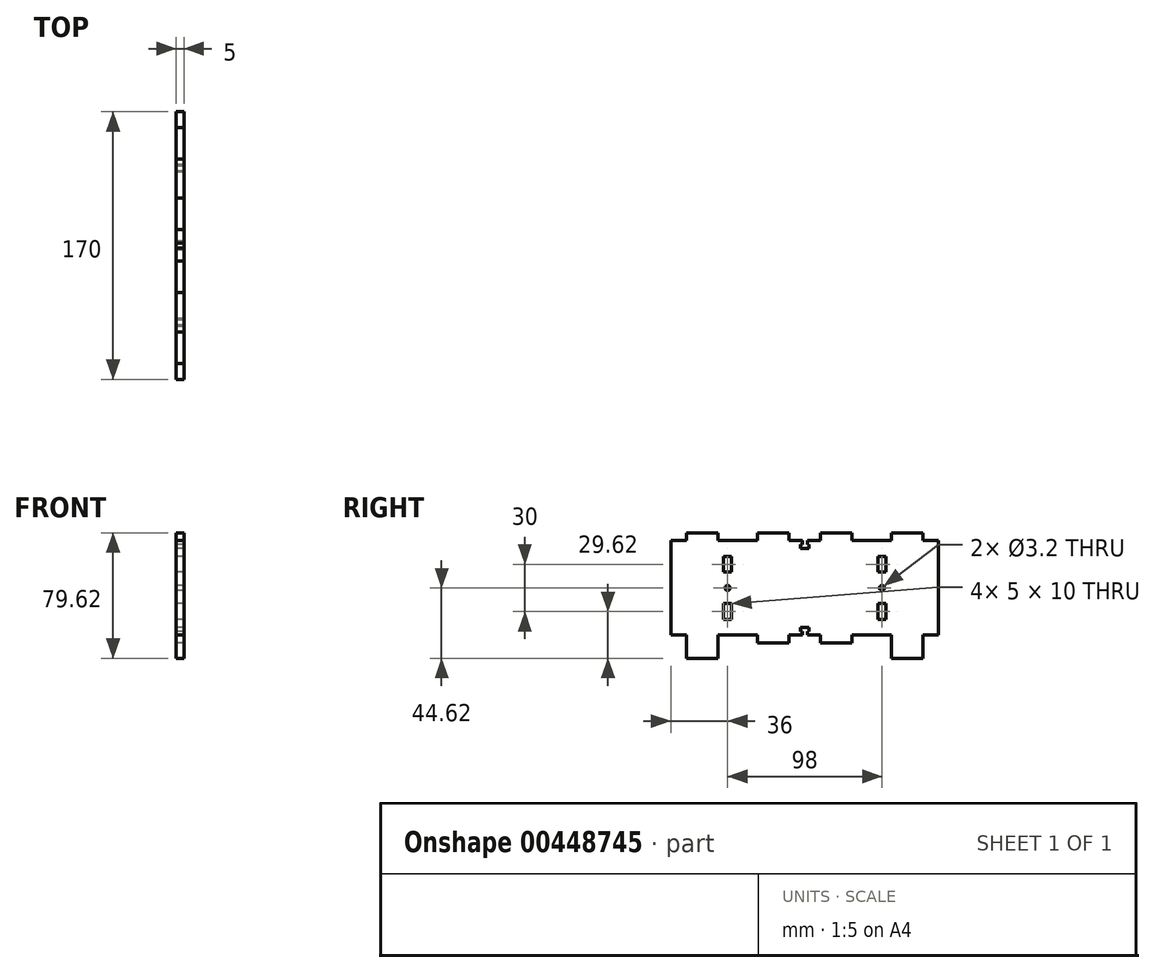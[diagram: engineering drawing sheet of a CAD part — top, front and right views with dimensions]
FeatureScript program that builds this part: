
annotation { "Feature Type Name" : "Feature", "Feature Type Description" : "" }
export const myFeature = defineFeature(function(context is Context, id is Id, definition is map)
    precondition{}
    {
        {
            assignVariable(context, id + "F0", {"name" : "thickness", "anyValue" : 5 * mm});
        }
        {
            var Q0;
            Q0=qCreatedBy(makeId("Right.planeOp"),FACE);
            var sketch = newSketch(context, id + "F1", { "sketchPlane" : qUnion([Q0])});
            skLineSegment(sketch, "E0.bottom", {"start": v(0, 0) * mm, "end": v(83.4, 0) * mm});
            skLineSegment(sketch, "E0.top", {"start": v(0, 60) * mm, "end": v(83.4, 60) * mm});
            skLineSegment(sketch, "E0.left", {"start": v(0, 0) * mm, "end": v(0, 60) * mm});
            skLineSegment(sketch, "E0.right", {"start": v(170, 0) * mm, "end": v(170, 60) * mm});
            skLineSegment(sketch, "E1", {"start": v(10, 0) * mm, "end": v(10, -14.62) * mm});
            skLineSegment(sketch, "E2", {"start": v(10, -14.62) * mm, "end": v(30, -14.62) * mm});
            skLineSegment(sketch, "E3", {"start": v(30, -14.62) * mm, "end": v(30, 0) * mm});
            skLineSegment(sketch, "E4", {"start": v(55, 0) * mm, "end": v(55, -5) * mm});
            skLineSegment(sketch, "E5", {"start": v(55, -5) * mm, "end": v(75, -5) * mm});
            skLineSegment(sketch, "E6", {"start": v(75, -5) * mm, "end": v(75, 0) * mm});
            skLineSegment(sketch, "E7", {"start": v(85, 60) * mm, "end": v(85, 0) * mm, "construction": true});
            skLineSegment(sketch, "E8.MirrorCS", {"start": v(95, -5) * mm, "end": v(95, 0) * mm});
            skLineSegment(sketch, "E9.MirrorCS", {"start": v(115, -5) * mm, "end": v(95, -5) * mm});
            skLineSegment(sketch, "E10.MirrorCS", {"start": v(115, 0) * mm, "end": v(115, -5) * mm});
            skLineSegment(sketch, "E11.MirrorCS", {"start": v(140, -14.62) * mm, "end": v(140, 0) * mm});
            skLineSegment(sketch, "E12.MirrorCS", {"start": v(160, -14.62) * mm, "end": v(140, -14.62) * mm});
            skLineSegment(sketch, "E13.MirrorCS", {"start": v(160, 0) * mm, "end": v(160, -14.62) * mm});
            skLineSegment(sketch, "E14", {"start": v(83.4, 0) * mm, "end": v(83.4, 2.5) * mm});
            skLineSegment(sketch, "E15", {"start": v(83.4, 2.5) * mm, "end": v(82.25, 2.5) * mm});
            skLineSegment(sketch, "E16", {"start": v(82.25, 2.5) * mm, "end": v(82.25, 5) * mm});
            skLineSegment(sketch, "E17", {"start": v(82.25, 5) * mm, "end": v(85, 5) * mm});
            skLineSegment(sketch, "E18.MirrorCS", {"start": v(86.6, 2.5) * mm, "end": v(87.75, 2.5) * mm});
            skLineSegment(sketch, "E19.MirrorCS", {"start": v(87.75, 5) * mm, "end": v(85, 5) * mm});
            skLineSegment(sketch, "E20.MirrorCS", {"start": v(87.75, 2.5) * mm, "end": v(87.75, 5) * mm});
            skLineSegment(sketch, "E21.MirrorCS", {"start": v(86.6, 0) * mm, "end": v(86.6, 2.5) * mm});
            skLineSegment(sketch, "E22", {"start": v(0, 30) * mm, "end": v(170, 30) * mm, "construction": true});
            skLineSegment(sketch, "E23.MirrorCS", {"start": v(83.4, 57.5) * mm, "end": v(82.25, 57.5) * mm});
            skLineSegment(sketch, "E24.MirrorCS", {"start": v(87.75, 57.5) * mm, "end": v(87.75, 55) * mm});
            skLineSegment(sketch, "E25.MirrorCS", {"start": v(86.6, 60) * mm, "end": v(86.6, 57.5) * mm});
            skLineSegment(sketch, "E26.MirrorCS", {"start": v(86.6, 57.5) * mm, "end": v(87.75, 57.5) * mm});
            skLineSegment(sketch, "E27.MirrorCS", {"start": v(82.25, 57.5) * mm, "end": v(82.25, 55) * mm});
            skLineSegment(sketch, "E28.MirrorCS", {"start": v(83.4, 60) * mm, "end": v(83.4, 57.5) * mm});
            skLineSegment(sketch, "E29.MirrorCS", {"start": v(82.25, 55) * mm, "end": v(85, 55) * mm});
            skLineSegment(sketch, "E30.MirrorCS", {"start": v(87.75, 55) * mm, "end": v(85, 55) * mm});
            skLineSegment(sketch, "E31.MirrorCS", {"start": v(95, 65) * mm, "end": v(95, 60) * mm});
            skLineSegment(sketch, "E32.MirrorCS", {"start": v(75, 65) * mm, "end": v(75, 60) * mm});
            skLineSegment(sketch, "E33.MirrorCS", {"start": v(55, 60) * mm, "end": v(55, 65) * mm});
            skLineSegment(sketch, "E34.MirrorCS", {"start": v(115, 60) * mm, "end": v(115, 65) * mm});
            skLineSegment(sketch, "E35.MirrorCS", {"start": v(115, 65) * mm, "end": v(95, 65) * mm});
            skLineSegment(sketch, "E36.MirrorCS", {"start": v(55, 65) * mm, "end": v(75, 65) * mm});
            skLineSegment(sketch, "E37", {"start": v(10, 60) * mm, "end": v(10, 65) * mm});
            skLineSegment(sketch, "E38", {"start": v(10, 65) * mm, "end": v(30, 65) * mm});
            skLineSegment(sketch, "E39", {"start": v(30, 65) * mm, "end": v(30, 60) * mm});
            skLineSegment(sketch, "E40.MirrorCS", {"start": v(140, 65) * mm, "end": v(140, 60) * mm});
            skLineSegment(sketch, "E41.MirrorCS", {"start": v(160, 60) * mm, "end": v(160, 65) * mm});
            skLineSegment(sketch, "E42.MirrorCS", {"start": v(160, 65) * mm, "end": v(140, 65) * mm});
            skLineSegment(sketch, "E43.trimOffspring", {"start": v(86.6, 0) * mm, "end": v(170, 0) * mm});
            skLineSegment(sketch, "E44.trimOffspring", {"start": v(86.6, 60) * mm, "end": v(170, 60) * mm});
            skLineSegment(sketch, "E45.bottom", {"start": v(33.5, 20) * mm, "end": v(38.5, 20) * mm});
            skLineSegment(sketch, "E45.top", {"start": v(33.5, 10) * mm, "end": v(38.5, 10) * mm});
            skLineSegment(sketch, "E45.left", {"start": v(33.5, 20) * mm, "end": v(33.5, 10) * mm});
            skLineSegment(sketch, "E45.right", {"start": v(38.5, 20) * mm, "end": v(38.5, 10) * mm});
            skCircle(sketch, "E46", {"center": v(36, 30) * mm, "radius": 1.6 * mm});
            skPoint(sketch, "E46.centerSnap0", {"position": v(36, 20) * mm});
            skLineSegment(sketch, "E47.MirrorCS", {"start": v(33.5, 40) * mm, "end": v(38.5, 40) * mm});
            skLineSegment(sketch, "E48.MirrorCS", {"start": v(38.5, 40) * mm, "end": v(38.5, 50) * mm});
            skLineSegment(sketch, "E49.MirrorCS", {"start": v(33.5, 50) * mm, "end": v(38.5, 50) * mm});
            skLineSegment(sketch, "E50.MirrorCS", {"start": v(33.5, 40) * mm, "end": v(33.5, 50) * mm});
            skCircle(sketch, "E51.MirrorC", {"center": v(134, 30) * mm, "radius": 1.6 * mm});
            skLineSegment(sketch, "E52.MirrorCS", {"start": v(136.5, 20) * mm, "end": v(131.5, 20) * mm});
            skLineSegment(sketch, "E53.MirrorCS", {"start": v(131.5, 20) * mm, "end": v(131.5, 10) * mm});
            skLineSegment(sketch, "E54.MirrorCS", {"start": v(136.5, 40) * mm, "end": v(131.5, 40) * mm});
            skLineSegment(sketch, "E55.MirrorCS", {"start": v(131.5, 40) * mm, "end": v(131.5, 50) * mm});
            skLineSegment(sketch, "E56.MirrorCS", {"start": v(136.5, 10) * mm, "end": v(131.5, 10) * mm});
            skLineSegment(sketch, "E57.MirrorCS", {"start": v(136.5, 40) * mm, "end": v(136.5, 50) * mm});
            skPoint(sketch, "E58.MirrorP", {"position": v(134, 20) * mm});
            skLineSegment(sketch, "E59.MirrorCS", {"start": v(136.5, 20) * mm, "end": v(136.5, 10) * mm});
            skLineSegment(sketch, "E60.MirrorCS", {"start": v(136.5, 50) * mm, "end": v(131.5, 50) * mm});
            skSolve(sketch);
        }
        {
            var Q0;
            Q0=qSketchRegion(id+"F1",true);
            extrude(context, id + "F2", {"entities" : qUnion([Q0]), "depth" : getVariable(context, 'thickness')});
        }
    });
